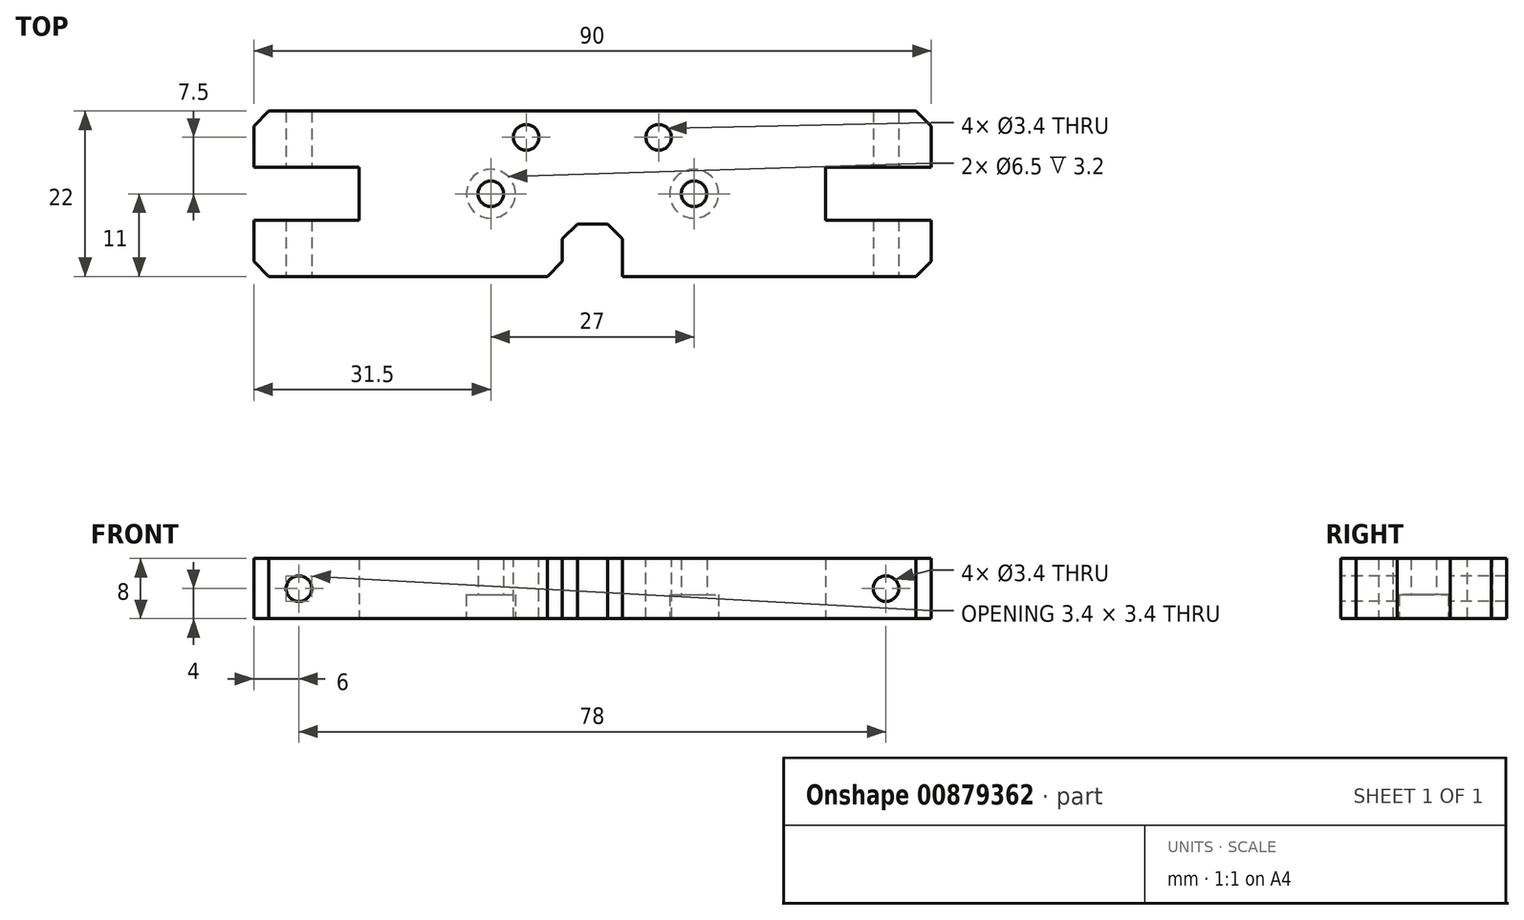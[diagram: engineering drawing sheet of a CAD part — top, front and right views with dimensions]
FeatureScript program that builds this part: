
annotation { "Feature Type Name" : "Feature", "Feature Type Description" : "" }
export const myFeature = defineFeature(function(context is Context, id is Id, definition is map)
    precondition{}
    {
        {
            var Q0;
            Q0=qCreatedBy(makeId("Top.planeOp"),FACE);
            var sketch = newSketch(context, id + "F0", { "sketchPlane" : qUnion([Q0])});
            skLineSegment(sketch, "E0.bottom", {"start": v(45, -11) * mm, "end": v(-45, -11) * mm});
            skLineSegment(sketch, "E0.top", {"start": v(45, 11) * mm, "end": v(-45, 11) * mm});
            skLineSegment(sketch, "E0.left", {"start": v(45, -11) * mm, "end": v(45, 11) * mm});
            skLineSegment(sketch, "E0.right", {"start": v(-45, -11) * mm, "end": v(-45, 11) * mm});
            skPoint(sketch, "E0.middle", {"position": v(0, 0) * mm});
            skLineSegment(sketch, "E1.bottom", {"start": v(-45, -3.5) * mm, "end": v(-31, -3.5) * mm});
            skLineSegment(sketch, "E1.top", {"start": v(-45, 3.5) * mm, "end": v(-31, 3.5) * mm});
            skLineSegment(sketch, "E1.left", {"start": v(-45, -3.5) * mm, "end": v(-45, 3.5) * mm});
            skLineSegment(sketch, "E1.right", {"start": v(-31, -3.5) * mm, "end": v(-31, 3.5) * mm});
            skPoint(sketch, "E1.middle", {"position": v(-38, 0) * mm});
            skLineSegment(sketch, "E2.bottom", {"start": v(45, -3.5) * mm, "end": v(31, -3.5) * mm});
            skLineSegment(sketch, "E2.top", {"start": v(45, 3.5) * mm, "end": v(31, 3.5) * mm});
            skLineSegment(sketch, "E2.left", {"start": v(45, -3.5) * mm, "end": v(45, 3.5) * mm});
            skLineSegment(sketch, "E2.right", {"start": v(31, -3.5) * mm, "end": v(31, 3.5) * mm});
            skPoint(sketch, "E2.middle", {"position": v(38, 0) * mm});
            skPoint(sketch, "E3", {"position": v(-13.5, 0) * mm});
            skPoint(sketch, "E4", {"position": v(13.5, 0) * mm});
            skSolve(sketch);
        }
        {
            var Q0;
            {var subQ6=sQuery(id+"F0.wireOp",EDGE,"E0.bottom");Q0=makeQuery(id+"F0.imprint","IMPRINT",FACE,{"disambiguationData":[TD([[makeQuery(id+"F0.imprint","IMPRINT",EDGE,{"derivedFrom":subQ6}),-1.0]])]});}
            extrude(context, id + "F1", {"entities" : qUnion([Q0]), "depth" : 8 * mm, "offsetDistance" : 25 * mm});
        }
        {
            var Q0;
            Q0=makeQuery(id+"F1.opExtrude","SWEPT_FACE",FACE,{"disambiguationData":[OSD([sQuery(id+"F0.wireOp",EDGE,"E0.bottom")])]});
            var sketch = newSketch(context, id + "F2", { "sketchPlane" : qUnion([Q0])});
            skPoint(sketch, "E5", {"position": v(-39, 4) * mm});
            skPoint(sketch, "E5.positionSnap0", {"position": v(-45, 4) * mm});
            skPoint(sketch, "E6", {"position": v(39, 4) * mm});
            skPoint(sketch, "E6.positionSnap0", {"position": v(45, 4) * mm});
            skSolve(sketch);
        }
        {
            var Q0;
            Q0=sQuery(id+"F2.wireOp",VERTEX,"E5");
            var Q1;
            Q1=sQuery(id+"F2.wireOp",VERTEX,"E6");
            var Q2;
            Q2=makeQuery(id+"F1.opExtrude","SWEPT_BODY",BODY,{"disambiguationData":[OSD([sQuery(id+"F0.wireOp",EDGE,"E0.bottom"),sQuery(id+"F0.wireOp",EDGE,"E0.top"),sQuery(id+"F0.wireOp",EDGE,"E0.left"),sQuery(id+"F0.wireOp",EDGE,"E0.right"),sQuery(id+"F0.wireOp",EDGE,"E1.bottom"),sQuery(id+"F0.wireOp",EDGE,"E1.top"),sQuery(id+"F0.wireOp",EDGE,"E1.right"),sQuery(id+"F0.wireOp",EDGE,"E2.bottom"),sQuery(id+"F0.wireOp",EDGE,"E2.top"),sQuery(id+"F0.wireOp",EDGE,"E2.right")])]});
            hole(context, id + "F3", {"style" : HoleStyle.SIMPLE, "endStyle" : HoleEndStyle.THROUGH, "holeDiameter" : 3.4 * mm, "majorDiameter" : 5 * mm, "isTappedThrough" : true, "tappedDepth" : 12 * mm, "tapClearance" : 3, "locations" : qUnion([Q0, Q1]), "scope" : qUnion([Q2])});
        }
        {
            var Q0;
            Q0=sQuery(id+"F0.wireOp",VERTEX,"E3");
            var Q1;
            Q1=sQuery(id+"F0.wireOp",VERTEX,"E4");
            var Q2;
            Q2=makeQuery(id+"F1.opExtrude","SWEPT_BODY",BODY,{"disambiguationData":[OSD([sQuery(id+"F0.wireOp",EDGE,"E0.bottom"),sQuery(id+"F0.wireOp",EDGE,"E0.top"),sQuery(id+"F0.wireOp",EDGE,"E0.left"),sQuery(id+"F0.wireOp",EDGE,"E0.right"),sQuery(id+"F0.wireOp",EDGE,"E1.bottom"),sQuery(id+"F0.wireOp",EDGE,"E1.top"),sQuery(id+"F0.wireOp",EDGE,"E1.right"),sQuery(id+"F0.wireOp",EDGE,"E2.bottom"),sQuery(id+"F0.wireOp",EDGE,"E2.top"),sQuery(id+"F0.wireOp",EDGE,"E2.right")])]});
            hole(context, id + "F4", {"style" : HoleStyle.C_BORE, "endStyle" : HoleEndStyle.THROUGH, "oppositeDirection" : true, "holeDiameter" : 3.4 * mm, "cBoreDiameter" : 6.5 * mm, "cBoreDepth" : 3.2 * mm, "majorDiameter" : 5 * mm, "isTappedThrough" : true, "tappedDepth" : 12 * mm, "tapClearance" : 3, "locations" : qUnion([Q0, Q1]), "scope" : qUnion([Q2])});
        }
        {
            var Q0;
            Q0=makeQuery(id+"F1.opExtrude","CAP_FACE",FACE,{"disambiguationData":[OSD([sQuery(id+"F0.wireOp",EDGE,"E0.bottom"),sQuery(id+"F0.wireOp",EDGE,"E0.top"),sQuery(id+"F0.wireOp",EDGE,"E0.left"),sQuery(id+"F0.wireOp",EDGE,"E0.right"),sQuery(id+"F0.wireOp",EDGE,"E1.bottom"),sQuery(id+"F0.wireOp",EDGE,"E1.top"),sQuery(id+"F0.wireOp",EDGE,"E1.right"),sQuery(id+"F0.wireOp",EDGE,"E2.bottom"),sQuery(id+"F0.wireOp",EDGE,"E2.top"),sQuery(id+"F0.wireOp",EDGE,"E2.right")])],"isStart":false});
            var sketch = newSketch(context, id + "F5", { "sketchPlane" : qUnion([Q0])});
            skPoint(sketch, "E7", {"position": v(-8.8, 7.5) * mm});
            skPoint(sketch, "E8", {"position": v(8.8, 7.5) * mm});
            skLineSegment(sketch, "E9.bottom", {"start": v(4, -11) * mm, "end": v(-4, -11) * mm});
            skLineSegment(sketch, "E9.top", {"start": v(4, -4) * mm, "end": v(-4, -4) * mm});
            skLineSegment(sketch, "E9.left", {"start": v(4, -11) * mm, "end": v(4, -4) * mm});
            skLineSegment(sketch, "E9.right", {"start": v(-4, -11) * mm, "end": v(-4, -4) * mm});
            skPoint(sketch, "E9.middle", {"position": v(0, -7.5) * mm});
            skSolve(sketch);
        }
        {
            var Q0;
            Q0=sQuery(id+"F5.wireOp",VERTEX,"E7");
            var Q1;
            Q1=sQuery(id+"F5.wireOp",VERTEX,"E8");
            var Q2;
            Q2=makeQuery(id+"F1.opExtrude","SWEPT_BODY",BODY,{"disambiguationData":[OSD([sQuery(id+"F0.wireOp",EDGE,"E0.bottom"),sQuery(id+"F0.wireOp",EDGE,"E0.top"),sQuery(id+"F0.wireOp",EDGE,"E0.left"),sQuery(id+"F0.wireOp",EDGE,"E0.right"),sQuery(id+"F0.wireOp",EDGE,"E1.bottom"),sQuery(id+"F0.wireOp",EDGE,"E1.top"),sQuery(id+"F0.wireOp",EDGE,"E1.right"),sQuery(id+"F0.wireOp",EDGE,"E2.bottom"),sQuery(id+"F0.wireOp",EDGE,"E2.top"),sQuery(id+"F0.wireOp",EDGE,"E2.right")])]});
            hole(context, id + "F6", {"style" : HoleStyle.SIMPLE, "endStyle" : HoleEndStyle.THROUGH, "holeDiameter" : 3.4 * mm, "majorDiameter" : 5 * mm, "isTappedThrough" : true, "tappedDepth" : 12 * mm, "tapClearance" : 3, "locations" : qUnion([Q0, Q1]), "scope" : qUnion([Q2])});
        }
        {
            var Q0;
            Q0=makeQuery(id+"F5.imprint","IMPRINT",FACE,{"disambiguationData":[TD([[makeQuery(id+"F5.imprint","IMPRINT",EDGE,{"derivedFrom":sQuery(id+"F5.wireOp",EDGE,"E9.bottom")}),-1.0]])]});
            extrude(context, id + "F7", {"entities" : qUnion([Q0]), "operationType" : NewBodyOperationType.REMOVE, "endBound" : BoundingType.UP_TO_NEXT, "oppositeDirection" : true, "depth" : 25 * mm, "offsetDistance" : 25 * mm});
        }
        {
            var Q0;
            Q0=makeQuery(id+"F1.opExtrude","SWEPT_EDGE",EDGE,{"disambiguationData":[OSD([sQuery(id+"F0.wireOp",EDGE,"E0.bottom"),sQuery(id+"F0.wireOp",EDGE,"E0.right")])]});
            var Q1;
            Q1=makeQuery(id+"F1.opExtrude","SWEPT_EDGE",EDGE,{"disambiguationData":[OSD([sQuery(id+"F0.wireOp",EDGE,"E0.bottom"),sQuery(id+"F0.wireOp",EDGE,"E0.left")])]});
            var Q2;
            Q2=makeQuery(id+"F7.boolean.opBoolean","COPY",EDGE,{"derivedFrom":makeQuery(id+"F7.opExtrude","SWEPT_EDGE",EDGE,{"disambiguationData":[OSD([sQuery(id+"F0.wireOp",EDGE,"E0.bottom"),sQuery(id+"F5.wireOp",EDGE,"E9.bottom"),sQuery(id+"F5.wireOp",EDGE,"E9.left")])]})});
            var Q3;
            Q3=makeQuery(id+"F7.boolean.opBoolean","COPY",EDGE,{"derivedFrom":makeQuery(id+"F7.opExtrude","SWEPT_EDGE",EDGE,{"disambiguationData":[OSD([sQuery(id+"F5.wireOp",EDGE,"E9.top"),sQuery(id+"F5.wireOp",EDGE,"E9.left")])]})});
            var Q4;
            Q4=makeQuery(id+"F7.boolean.opBoolean","COPY",EDGE,{"derivedFrom":makeQuery(id+"F7.opExtrude","SWEPT_EDGE",EDGE,{"disambiguationData":[OSD([sQuery(id+"F5.wireOp",EDGE,"E9.top"),sQuery(id+"F5.wireOp",EDGE,"E9.right")])]})});
            var Q5;
            Q5=makeQuery(id+"F7.boolean.opBoolean","COPY",EDGE,{"derivedFrom":makeQuery(id+"F7.opExtrude","SWEPT_EDGE",EDGE,{"disambiguationData":[OSD([sQuery(id+"F0.wireOp",EDGE,"E0.bottom"),sQuery(id+"F5.wireOp",EDGE,"E9.bottom"),sQuery(id+"F5.wireOp",EDGE,"E9.right")])]})});
            var Q6;
            Q6=makeQuery(id+"F1.opExtrude","SWEPT_EDGE",EDGE,{"disambiguationData":[OSD([sQuery(id+"F0.wireOp",EDGE,"E0.top"),sQuery(id+"F0.wireOp",EDGE,"E0.left")])]});
            var Q7;
            Q7=makeQuery(id+"F1.opExtrude","SWEPT_EDGE",EDGE,{"disambiguationData":[OSD([sQuery(id+"F0.wireOp",EDGE,"E0.top"),sQuery(id+"F0.wireOp",EDGE,"E0.right")])]});
            chamfer(context, id + "F8", {"entities" : qUnion([Q0, Q1, Q2, Q3, Q4, Q5, Q6, Q7]), "width" : 2 * mm, "tangentPropagation" : true});
        }
    });
